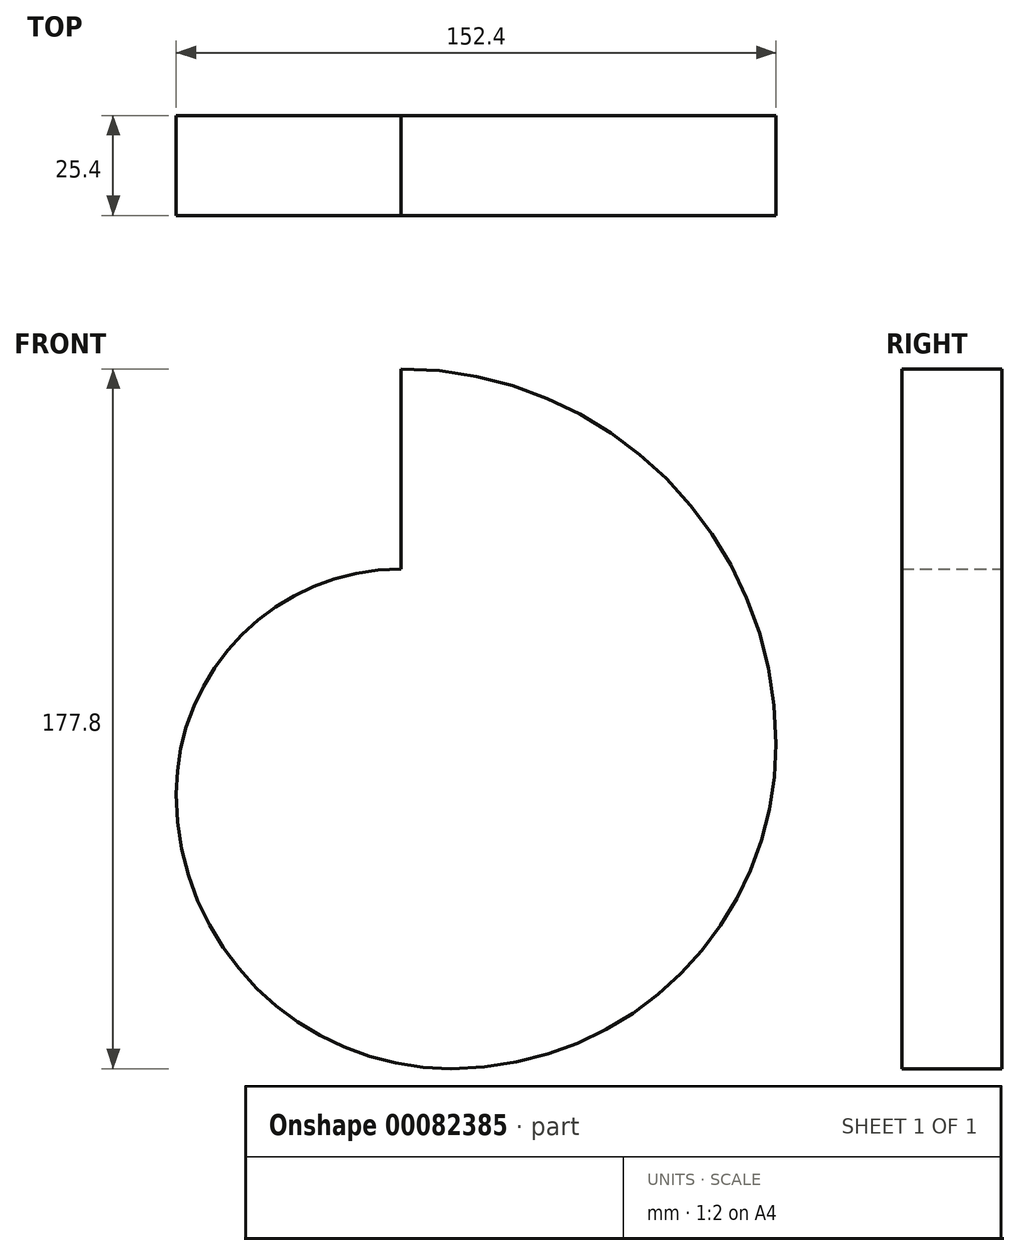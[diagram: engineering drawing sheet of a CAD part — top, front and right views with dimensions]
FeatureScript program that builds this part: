
annotation { "Feature Type Name" : "Feature", "Feature Type Description" : "" }
export const myFeature = defineFeature(function(context is Context, id is Id, definition is map)
    precondition{}
    {
        {
            var Q0;
            Q0=qCreatedBy(makeId("Front.planeOp"),FACE);
            var sketch = newSketch(context, id + "F0", { "sketchPlane" : qUnion([Q0])});
            skLineSegment(sketch, "E0.bottom", {"start": v(76.2, 88.9) * mm, "end": v(-76.2, 88.9) * mm, "construction": true});
            skLineSegment(sketch, "E0.top", {"start": v(76.2, -88.9) * mm, "end": v(-76.2, -88.9) * mm, "construction": true});
            skLineSegment(sketch, "E0.left", {"start": v(76.2, 88.9) * mm, "end": v(76.2, -88.9) * mm, "construction": true});
            skLineSegment(sketch, "E0.right", {"start": v(-76.2, 88.9) * mm, "end": v(-76.2, -88.9) * mm, "construction": true});
            skPoint(sketch, "E0.middle", {"position": v(0, 0) * mm});
            skLineSegment(sketch, "E1", {"start": v(-76.2, 38.1) * mm, "end": v(76.2, 38.1) * mm, "construction": true});
            skLineSegment(sketch, "E2.bottom", {"start": v(31.75, 38.1) * mm, "end": v(-44.45, 38.1) * mm, "construction": true});
            skLineSegment(sketch, "E2.top", {"start": v(31.75, -50.8) * mm, "end": v(-44.45, -50.8) * mm, "construction": true});
            skLineSegment(sketch, "E2.left", {"start": v(31.75, 38.1) * mm, "end": v(31.75, -50.8) * mm, "construction": true});
            skLineSegment(sketch, "E2.right", {"start": v(-44.45, 38.1) * mm, "end": v(-44.45, -50.8) * mm, "construction": true});
            skLineSegment(sketch, "E3.bottom", {"start": v(-28.58, 20.72) * mm, "end": v(9.52, 20.72) * mm, "construction": true});
            skLineSegment(sketch, "E3.top", {"start": v(-28.58, -23.73) * mm, "end": v(9.52, -23.73) * mm, "construction": true});
            skLineSegment(sketch, "E3.left", {"start": v(-28.58, 20.72) * mm, "end": v(-28.58, -23.73) * mm, "construction": true});
            skLineSegment(sketch, "E3.right", {"start": v(9.52, 20.72) * mm, "end": v(9.52, -23.73) * mm, "construction": true});
            skLineSegment(sketch, "E4", {"start": v(-28.58, 8.02) * mm, "end": v(9.52, 8.02) * mm, "construction": true});
            skLineSegment(sketch, "E5", {"start": v(-76.2, 38.1) * mm, "end": v(-12.7, -25.4) * mm, "construction": true});
            skLineSegment(sketch, "E6", {"start": v(-76.2, -88.9) * mm, "end": v(-11.03, -23.73) * mm, "construction": true});
            skLineSegment(sketch, "E7", {"start": v(76.2, 88.9) * mm, "end": v(-76.2, -63.5) * mm, "construction": true});
            skLineSegment(sketch, "E8", {"start": v(76.2, -88.9) * mm, "end": v(-76.2, 63.5) * mm, "construction": true});
            skLineSegment(sketch, "E9", {"start": v(-25.4, -12.7) * mm, "end": v(-12.7, 0) * mm, "construction": true});
            skLineSegment(sketch, "E10", {"start": v(-25.4, -12.7) * mm, "end": v(-12.7, -25.4) * mm, "construction": true});
            skLineSegment(sketch, "E11", {"start": v(-12.7, -25.4) * mm, "end": v(0, -12.7) * mm, "construction": true});
            skLineSegment(sketch, "E12", {"start": v(0, -12.7) * mm, "end": v(-12.7, 0) * mm, "construction": true});
            skLineSegment(sketch, "E13", {"start": v(-19.05, -6.35) * mm, "end": v(-19.05, 38.1) * mm, "construction": true});
            skLineSegment(sketch, "E14", {"start": v(-6.35, -6.35) * mm, "end": v(76.2, -6.35) * mm, "construction": true});
            skPoint(sketch, "E14.endSnap0", {"position": v(31.75, -6.35) * mm});
            skLineSegment(sketch, "E15", {"start": v(-6.35, -19.05) * mm, "end": v(-6.35, -88.9) * mm, "construction": true});
            skPoint(sketch, "E15.endSnap0", {"position": v(0, -88.9) * mm});
            skLineSegment(sketch, "E16", {"start": v(-19.05, -19.05) * mm, "end": v(-76.2, -19.05) * mm, "construction": true});
            skLineSegment(sketch, "E17.bottom", {"start": v(-19.05, -6.35) * mm, "end": v(-6.35, -6.35) * mm});
            skLineSegment(sketch, "E17.top", {"start": v(-19.05, -19.05) * mm, "end": v(-6.35, -19.05) * mm});
            skLineSegment(sketch, "E17.left", {"start": v(-19.05, -6.35) * mm, "end": v(-19.05, -19.05) * mm});
            skLineSegment(sketch, "E17.right", {"start": v(-6.35, -6.35) * mm, "end": v(-6.35, -19.05) * mm});
            skArc(sketch, "E18", {"start": v(-19.05, 38.1) * mm, "mid": v(-59.46, 21.36) * mm, "end": v(-76.2, -19.05) * mm});
            skArc(sketch, "E19", {"start": v(-76.2, -19.05) * mm, "mid": v(-55.74, -68.44) * mm, "end": v(-6.35, -88.9) * mm});
            skArc(sketch, "E20", {"start": v(-6.35, -88.9) * mm, "mid": v(52.02, -64.72) * mm, "end": v(76.2, -6.35) * mm});
            skArc(sketch, "E21", {"start": v(76.2, -6.35) * mm, "mid": v(48.3, 61) * mm, "end": v(-19.05, 88.9) * mm});
            skLineSegment(sketch, "E22", {"start": v(-19.05, 88.9) * mm, "end": v(-19.05, 38.1) * mm});
            skSolve(sketch);
        }
        {
            var Q0;
            Q0=makeQuery(id+"F0.imprint","IMPRINT",FACE,{"disambiguationData":[TD([[makeQuery(id+"F0.imprint","IMPRINT",EDGE,{"derivedFrom":sQuery(id+"F0.wireOp",EDGE,"E17.bottom")}),1.0]])]});
            var Q1;
            Q1=makeQuery(id+"F0.imprint","IMPRINT",FACE,{"disambiguationData":[TD([[makeQuery(id+"F0.imprint","IMPRINT",EDGE,{"derivedFrom":sQuery(id+"F0.wireOp",EDGE,"E17.bottom")}),-1.0]])]});
            extrude(context, id + "F1", {"entities" : qUnion([Q0, Q1]), "depth" : 25.4 * mm});
        }
    });
